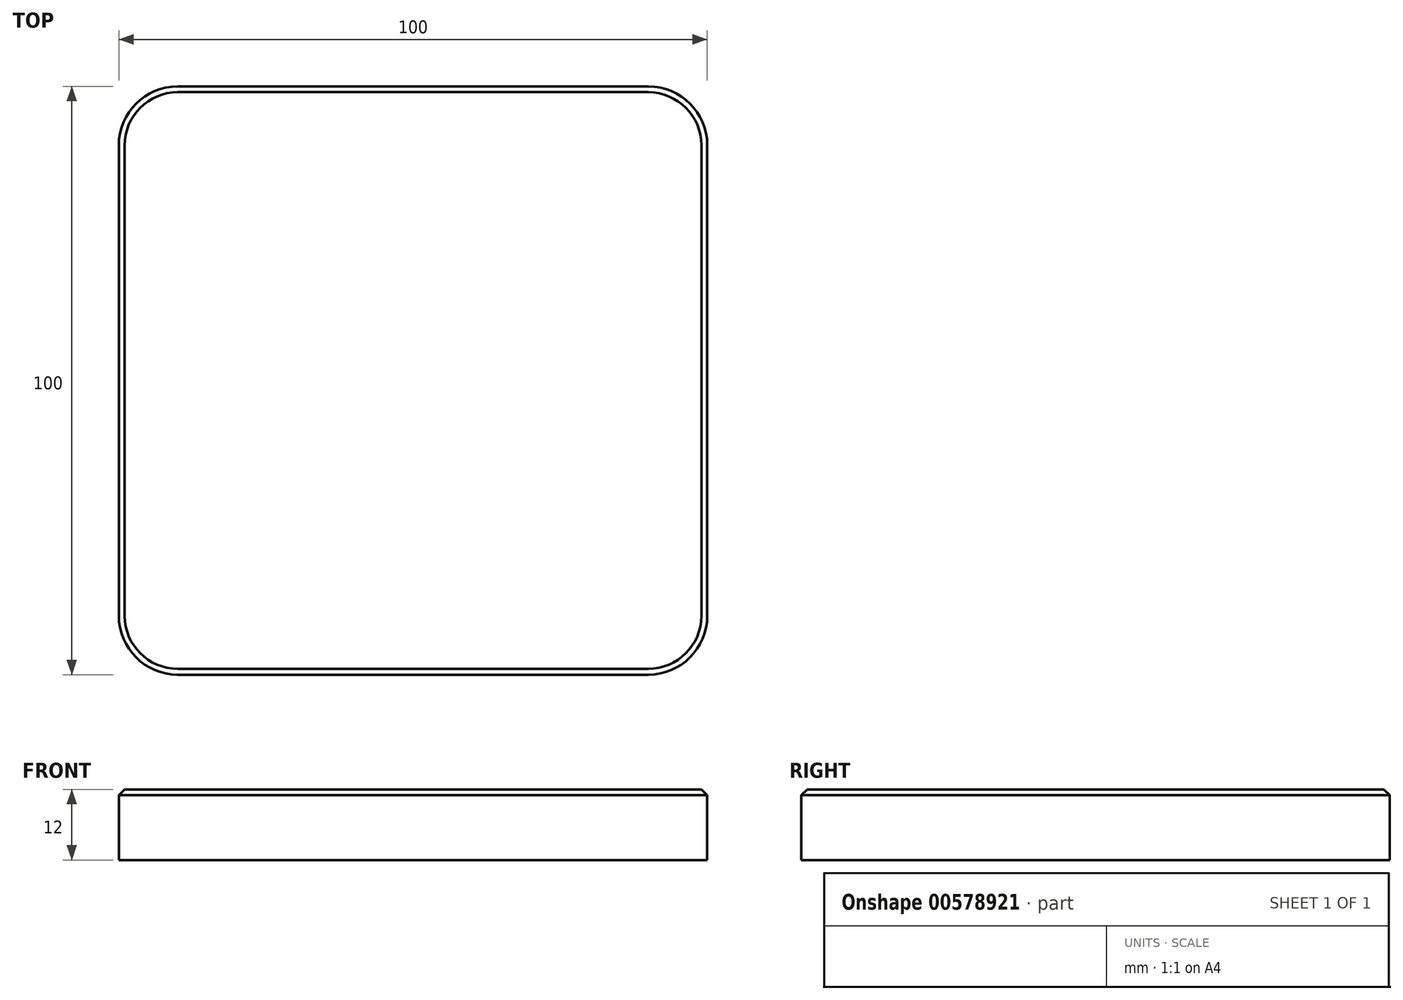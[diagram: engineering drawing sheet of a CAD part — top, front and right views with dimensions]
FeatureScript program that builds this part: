
annotation { "Feature Type Name" : "Feature", "Feature Type Description" : "" }
export const myFeature = defineFeature(function(context is Context, id is Id, definition is map)
    precondition{}
    {
        {
            var Q0;
            Q0=qCreatedBy(makeId("Top.planeOp"),FACE);
            var sketch = newSketch(context, id + "F0", { "sketchPlane" : qUnion([Q0])});
            skLineSegment(sketch, "E0.bottom", {"start": v(40, 50) * mm, "end": v(-40, 50) * mm});
            skLineSegment(sketch, "E0.top", {"start": v(40, -50) * mm, "end": v(-40, -50) * mm});
            skLineSegment(sketch, "E0.left", {"start": v(50, 40) * mm, "end": v(50, -40) * mm});
            skLineSegment(sketch, "E0.right", {"start": v(-50, 40) * mm, "end": v(-50, -40) * mm});
            skPoint(sketch, "E0.middle", {"position": v(0, 0) * mm});
            skPoint(sketch, "E1.visualSharp", {"position": v(50, 50) * mm});
            skArc(sketch, "E1.filletArc", {"start": v(50, 40) * mm, "mid": v(47.07, 47.07) * mm, "end": v(40, 50) * mm});
            skPoint(sketch, "E2.visualSharp", {"position": v(50, -50) * mm});
            skArc(sketch, "E2.filletArc", {"start": v(40, -50) * mm, "mid": v(47.07, -47.07) * mm, "end": v(50, -40) * mm});
            skPoint(sketch, "E3.visualSharp", {"position": v(-50, -50) * mm});
            skArc(sketch, "E3.filletArc", {"start": v(-50, -40) * mm, "mid": v(-47.07, -47.07) * mm, "end": v(-40, -50) * mm});
            skPoint(sketch, "E4.visualSharp", {"position": v(-50, 50) * mm});
            skArc(sketch, "E4.filletArc", {"start": v(-40, 50) * mm, "mid": v(-47.07, 47.07) * mm, "end": v(-50, 40) * mm});
            skSolve(sketch);
        }
        {
            var Q0;
            Q0 = qSketchRegion(id + "F0", true);
            extrude(context, id + "F1", {"entities" : qUnion([Q0]), "depth" : 12 * mm, "offsetDistance" : 25 * mm});
        }
        {
            var Q0;
            Q0=makeQuery(id+"F1.opExtrude","CAP_FACE",FACE,{"disambiguationData":[OSD([sQuery(id+"F0.wireOp",EDGE,"E0.bottom"),sQuery(id+"F0.wireOp",EDGE,"E0.top"),sQuery(id+"F0.wireOp",EDGE,"E0.left"),sQuery(id+"F0.wireOp",EDGE,"E0.right"),sQuery(id+"F0.wireOp",EDGE,"E1.filletArc"),sQuery(id+"F0.wireOp",EDGE,"E2.filletArc"),sQuery(id+"F0.wireOp",EDGE,"E3.filletArc"),sQuery(id+"F0.wireOp",EDGE,"E4.filletArc")])],"isStart":false});
            chamfer(context, id + "F2", {"entities" : qUnion([Q0]), "width" : 1 * mm, "tangentPropagation" : true});
        }
    });
